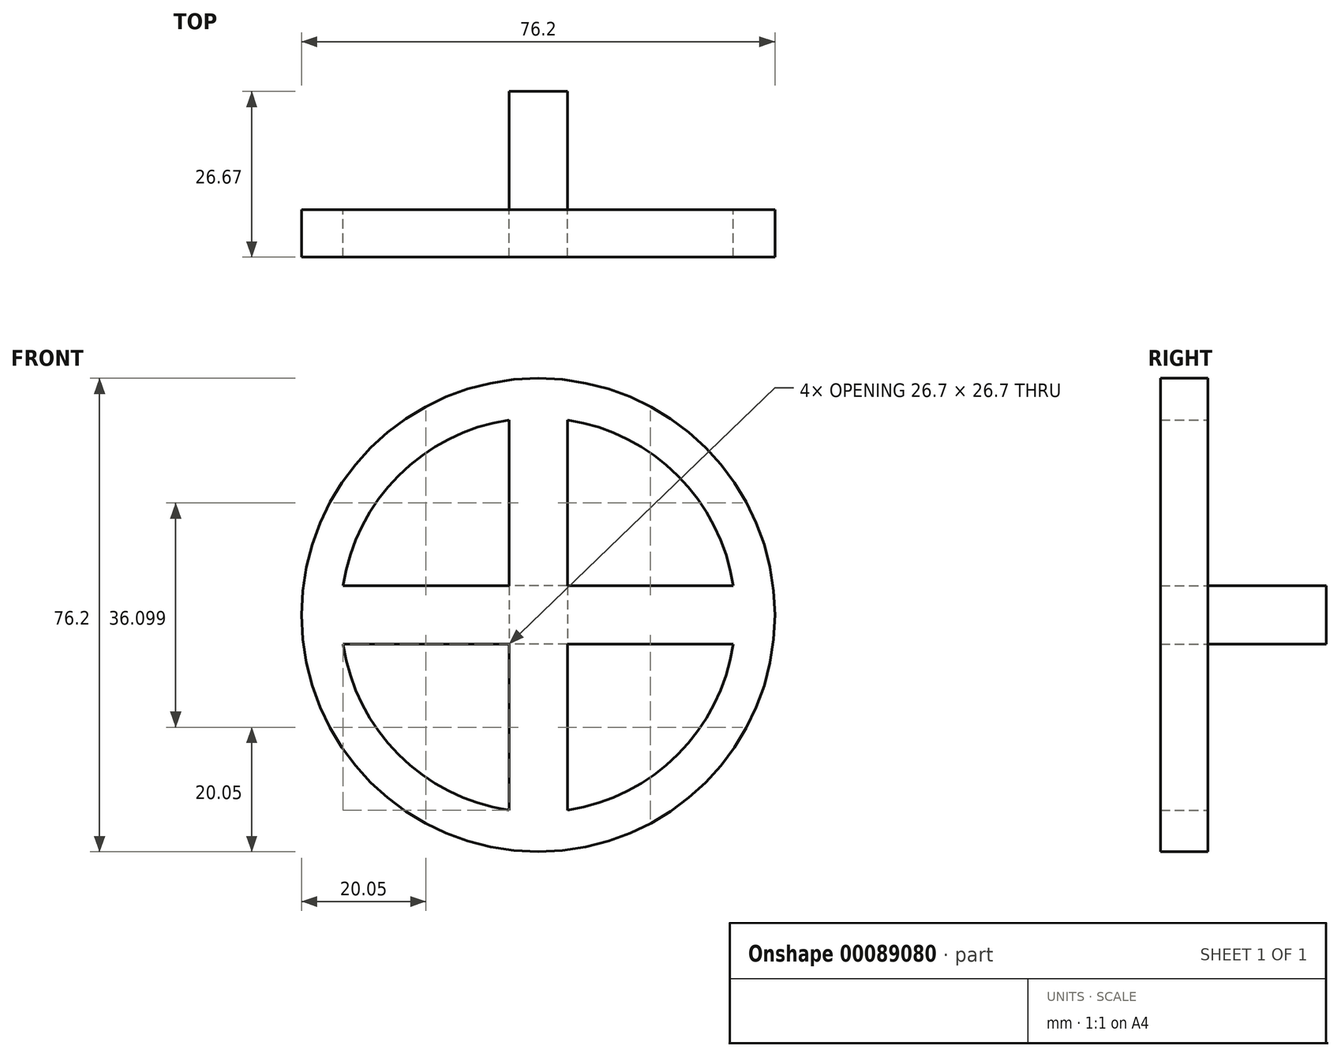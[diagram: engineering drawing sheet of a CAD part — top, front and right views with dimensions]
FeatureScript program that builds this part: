
annotation { "Feature Type Name" : "Feature", "Feature Type Description" : "" }
export const myFeature = defineFeature(function(context is Context, id is Id, definition is map)
    precondition{}
    {
        {
            var Q0;
            Q0=qCreatedBy(makeId("Front.planeOp"),FACE);
            var sketch = newSketch(context, id + "F0", { "sketchPlane" : qUnion([Q0])});
            skLineSegment(sketch, "E0.bottom", {"start": v(4.7, 4.7) * mm, "end": v(-4.7, 4.7) * mm});
            skLineSegment(sketch, "E0.top", {"start": v(4.7, -4.7) * mm, "end": v(-4.7, -4.7) * mm});
            skLineSegment(sketch, "E0.left", {"start": v(4.7, 4.7) * mm, "end": v(4.7, -4.7) * mm});
            skLineSegment(sketch, "E0.right", {"start": v(-4.7, 4.7) * mm, "end": v(-4.7, -4.7) * mm});
            skPoint(sketch, "E0.middle", {"position": v(0, 0) * mm});
            skSolve(sketch);
        }
        {
            var Q0;
            Q0 = qSketchRegion(id + "F0", true);
            extrude(context, id + "F1", {"entities" : qUnion([Q0]), "depth" : 19.05 * mm});
        }
        {
            var Q0;
            Q0=makeQuery(id+"F1.opExtrude","CAP_FACE",FACE,{"disambiguationData":[OSD([sQuery(id+"F0.wireOp",EDGE,"E0.bottom"),sQuery(id+"F0.wireOp",EDGE,"E0.top"),sQuery(id+"F0.wireOp",EDGE,"E0.left"),sQuery(id+"F0.wireOp",EDGE,"E0.right")])],"isStart":false});
            var sketch = newSketch(context, id + "F2", { "sketchPlane" : qUnion([Q0])});
            skCircle(sketch, "E1", {"center": v(0, 0) * mm, "radius": 38.1 * mm});
            skArc(sketch, "E2", {"start": v(-4.7, 31.4) * mm, "mid": v(-22.45, 22.45) * mm, "end": v(-31.4, 4.7) * mm});
            skLineSegment(sketch, "E3", {"start": v(-4.7, 4.7) * mm, "end": v(-4.7, 31.4) * mm});
            skLineSegment(sketch, "E4", {"start": v(4.7, 4.7) * mm, "end": v(4.7, 31.4) * mm});
            skLineSegment(sketch, "E5", {"start": v(-4.7, -4.7) * mm, "end": v(-31.4, -4.7) * mm});
            skLineSegment(sketch, "E6", {"start": v(-4.7, 4.7) * mm, "end": v(-31.4, 4.7) * mm});
            skLineSegment(sketch, "E7", {"start": v(4.7, -4.7) * mm, "end": v(4.7, -31.4) * mm});
            skLineSegment(sketch, "E8", {"start": v(4.7, -4.7) * mm, "end": v(31.4, -4.7) * mm});
            skLineSegment(sketch, "E9", {"start": v(4.7, 4.7) * mm, "end": v(31.4, 4.7) * mm});
            skArc(sketch, "E10.trimOffspring", {"start": v(-31.4, -4.7) * mm, "mid": v(-22.45, -22.45) * mm, "end": v(-4.7, -31.4) * mm});
            skArc(sketch, "E11.trimOffspring", {"start": v(4.7, -31.4) * mm, "mid": v(22.45, -22.45) * mm, "end": v(31.4, -4.7) * mm});
            skArc(sketch, "E12.trimOffspring", {"start": v(31.4, 4.7) * mm, "mid": v(22.45, 22.45) * mm, "end": v(4.7, 31.4) * mm});
            skLineSegment(sketch, "E13", {"start": v(-4.7, -4.7) * mm, "end": v(-4.7, -31.4) * mm});
            skSolve(sketch);
        }
        {
            var Q0;
            Q0 = qSketchRegion(id + "F2", true);
            extrude(context, id + "F3", {"entities" : qUnion([Q0]), "operationType" : NewBodyOperationType.ADD, "depth" : 7.62 * mm});
        }
    });
